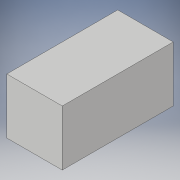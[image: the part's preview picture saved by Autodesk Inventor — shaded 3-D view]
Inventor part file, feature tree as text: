
AUTODESK INVENTOR PART (.ipt)
format: ipt  version: 2017 (Build 210142000, 142)  size: 89,600 bytes
history: native  units: in
note: dims shown in document units (in); Inventor stores cm internally (conversion verified against a paired STEP export)
features: extrude x1, sketch x1
ambient origin geometry x8: Origin, YZ Plane, XZ Plane, XY Plane, X Axis, Y Axis, Z Axis, Center Point
bodies: Solid1 (feature_tree)
feature tree (2):
  extrude  "Extrusion1"  Depth=4.0in
  sketch  "Sketch1"  dims[d0=2.0in d1=4.0in d2=2.0in d3=0.0in]
